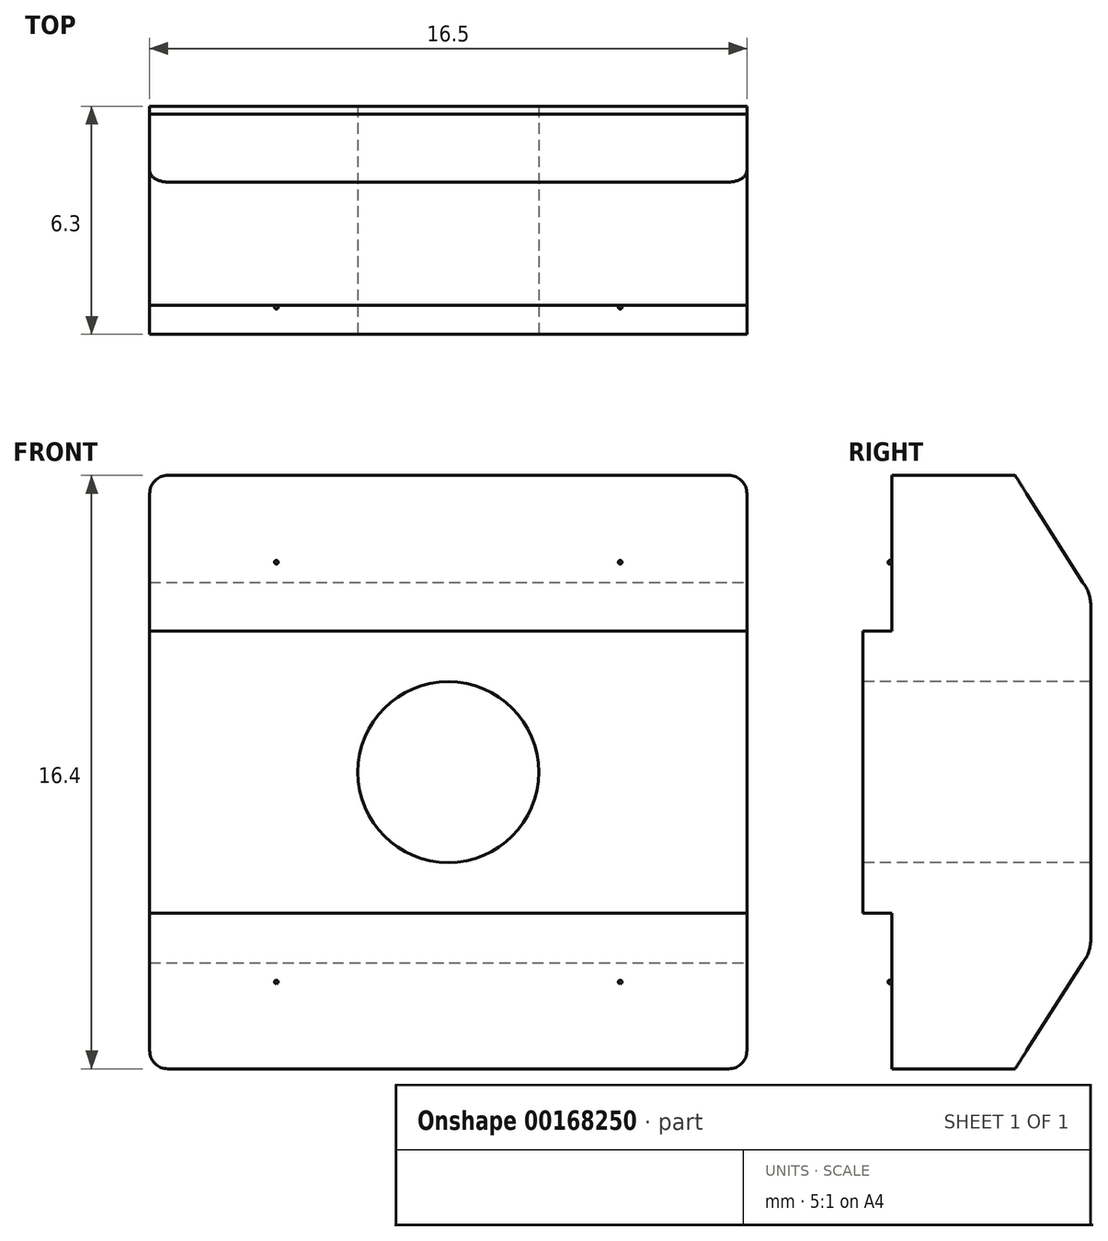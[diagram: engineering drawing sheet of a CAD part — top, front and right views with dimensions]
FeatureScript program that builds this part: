
annotation { "Feature Type Name" : "Feature", "Feature Type Description" : "" }
export const myFeature = defineFeature(function(context is Context, id is Id, definition is map)
    precondition{}
    {
        {
            var Q0;
            Q0=qCreatedBy(makeId("Front.planeOp"),FACE);
            var sketch = newSketch(context, id + "F0", { "sketchPlane" : qUnion([Q0])});
            skLineSegment(sketch, "E0", {"start": v(-32.08, -36.88) * mm, "end": v(-18.08, -36.88) * mm});
            skCircle(sketch, "E1", {"center": v(-25.08, -44.38) * mm, "radius": 1.5 * mm});
            skLineSegment(sketch, "E2", {"start": v(-32.08, -40.48) * mm, "end": v(-18.08, -40.48) * mm});
            skLineSegment(sketch, "E3", {"start": v(-32.08, -48.28) * mm, "end": v(-18.08, -48.28) * mm});
            skLineSegment(sketch, "E4", {"start": v(-18.08, -51.88) * mm, "end": v(-32.08, -51.88) * mm});
            skLineSegment(sketch, "E5", {"start": v(-35.33, -44.38) * mm, "end": v(-14.83, -44.38) * mm});
            skLineSegment(sketch, "E6", {"start": v(-32.08, -51.88) * mm, "end": v(-32.08, -36.88) * mm});
            skLineSegment(sketch, "E7", {"start": v(-25.08, -34.18) * mm, "end": v(-25.08, -54.58) * mm});
            skCircle(sketch, "E8", {"center": v(-25.08, -44.38) * mm, "radius": 1.23 * mm});
            skLineSegment(sketch, "E9", {"start": v(-18.08, -51.88) * mm, "end": v(-18.08, -36.88) * mm});
            skLineSegment(sketch, "E10", {"start": v(-33.33, -52.08) * mm, "end": v(-33.33, -36.68) * mm});
            skLineSegment(sketch, "E11", {"start": v(-16.83, -36.68) * mm, "end": v(-16.83, -52.08) * mm});
            skLineSegment(sketch, "E12", {"start": v(-17.33, -52.58) * mm, "end": v(-32.83, -52.58) * mm});
            skLineSegment(sketch, "E13", {"start": v(-32.83, -36.18) * mm, "end": v(-17.33, -36.18) * mm});
            skArc(sketch, "E14", {"start": v(-33.33, -52.08) * mm, "mid": v(-33.19, -52.43) * mm, "end": v(-32.83, -52.58) * mm});
            skArc(sketch, "E15", {"start": v(-17.33, -52.58) * mm, "mid": v(-16.98, -52.43) * mm, "end": v(-16.83, -52.08) * mm});
            skArc(sketch, "E16", {"start": v(-16.83, -36.68) * mm, "mid": v(-16.98, -36.33) * mm, "end": v(-17.33, -36.18) * mm});
            skArc(sketch, "E17", {"start": v(-32.83, -36.18) * mm, "mid": v(-33.19, -36.33) * mm, "end": v(-33.33, -36.68) * mm});
            skArc(sketch, "E18", {"start": v(27.03, -48.08) * mm, "mid": v(27.1, -48.22) * mm, "end": v(27.23, -48.28) * mm});
            skLineSegment(sketch, "E19", {"start": v(27.83, -52.58) * mm, "end": v(27.83, -36.18) * mm});
            skLineSegment(sketch, "E20", {"start": v(31.24, -36.18) * mm, "end": v(31.24, -52.58) * mm});
            skLineSegment(sketch, "E21", {"start": v(33.33, -49.02) * mm, "end": v(33.33, -39.76) * mm});
            skLineSegment(sketch, "E22", {"start": v(31.54, -51.6) * mm, "end": v(33.11, -49.65) * mm});
            skArc(sketch, "E23", {"start": v(33.11, -49.65) * mm, "mid": v(33.28, -49.35) * mm, "end": v(33.33, -49.02) * mm});
            skLineSegment(sketch, "E24", {"start": v(27.83, -52.58) * mm, "end": v(31.24, -52.58) * mm});
            skArc(sketch, "E25", {"start": v(31.24, -51.86) * mm, "mid": v(31.4, -51.75) * mm, "end": v(31.54, -51.6) * mm});
            skLineSegment(sketch, "E26", {"start": v(27.83, -48.28) * mm, "end": v(27.23, -48.28) * mm});
            skLineSegment(sketch, "E27", {"start": v(33.11, -39.13) * mm, "end": v(31.54, -37.16) * mm});
            skLineSegment(sketch, "E28", {"start": v(35.33, -44.38) * mm, "end": v(25.03, -44.38) * mm});
            skArc(sketch, "E29", {"start": v(33.33, -39.76) * mm, "mid": v(33.28, -39.43) * mm, "end": v(33.11, -39.13) * mm});
            skLineSegment(sketch, "E30", {"start": v(27.03, -48.08) * mm, "end": v(27.03, -40.68) * mm});
            skLineSegment(sketch, "E31", {"start": v(27.83, -36.18) * mm, "end": v(31.24, -36.18) * mm});
            skArc(sketch, "E32", {"start": v(31.54, -37.16) * mm, "mid": v(31.4, -37.02) * mm, "end": v(31.24, -36.9) * mm});
            skArc(sketch, "E33", {"start": v(27.23, -40.48) * mm, "mid": v(27.1, -40.54) * mm, "end": v(27.03, -40.68) * mm});
            skLineSegment(sketch, "E34", {"start": v(27.83, -40.48) * mm, "end": v(27.23, -40.48) * mm});
            skArc(sketch, "E35", {"start": v(27.03, -13.08) * mm, "mid": v(27.1, -13.22) * mm, "end": v(27.23, -13.28) * mm});
            skLineSegment(sketch, "E36", {"start": v(27.83, -17.58) * mm, "end": v(27.83, -1.18) * mm});
            skLineSegment(sketch, "E37", {"start": v(31.24, -1.18) * mm, "end": v(31.24, -17.58) * mm});
            skLineSegment(sketch, "E38", {"start": v(33.33, -14.02) * mm, "end": v(33.33, -4.76) * mm});
            skArc(sketch, "E39", {"start": v(31.24, -16.86) * mm, "mid": v(31.4, -16.75) * mm, "end": v(31.54, -16.6) * mm});
            skLineSegment(sketch, "E40", {"start": v(27.83, -13.28) * mm, "end": v(27.23, -13.28) * mm});
            skLineSegment(sketch, "E41", {"start": v(27.83, -17.58) * mm, "end": v(31.24, -17.58) * mm});
            skLineSegment(sketch, "E42", {"start": v(31.54, -16.6) * mm, "end": v(33.11, -14.65) * mm});
            skArc(sketch, "E43", {"start": v(33.11, -14.65) * mm, "mid": v(33.28, -14.35) * mm, "end": v(33.33, -14.02) * mm});
            skArc(sketch, "E44", {"start": v(31.54, -2.16) * mm, "mid": v(31.4, -2.02) * mm, "end": v(31.24, -1.9) * mm});
            skLineSegment(sketch, "E45", {"start": v(35.33, -9.38) * mm, "end": v(25.03, -9.38) * mm});
            skLineSegment(sketch, "E46", {"start": v(27.03, -13.08) * mm, "end": v(27.03, -5.68) * mm});
            skArc(sketch, "E47", {"start": v(27.23, -5.48) * mm, "mid": v(27.1, -5.54) * mm, "end": v(27.03, -5.68) * mm});
            skLineSegment(sketch, "E48", {"start": v(27.83, -5.48) * mm, "end": v(27.23, -5.48) * mm});
            skLineSegment(sketch, "E49", {"start": v(27.83, -1.18) * mm, "end": v(31.24, -1.18) * mm});
            skLineSegment(sketch, "E50", {"start": v(33.11, -4.13) * mm, "end": v(31.54, -2.16) * mm});
            skArc(sketch, "E51", {"start": v(33.33, -4.76) * mm, "mid": v(33.28, -4.43) * mm, "end": v(33.11, -4.13) * mm});
            skLineSegment(sketch, "E52", {"start": v(-25.08, 0.82) * mm, "end": v(-25.08, -19.58) * mm});
            skLineSegment(sketch, "E53", {"start": v(-32.83, -1.18) * mm, "end": v(-17.33, -1.18) * mm});
            skLineSegment(sketch, "E54", {"start": v(-17.33, -17.58) * mm, "end": v(-32.83, -17.58) * mm});
            skLineSegment(sketch, "E55", {"start": v(-35.33, -9.38) * mm, "end": v(-14.83, -9.38) * mm});
            skLineSegment(sketch, "E56", {"start": v(-18.08, -16.88) * mm, "end": v(-32.08, -16.88) * mm});
            skLineSegment(sketch, "E57", {"start": v(-32.08, -13.28) * mm, "end": v(-18.08, -13.28) * mm});
            skLineSegment(sketch, "E58", {"start": v(-32.08, -5.48) * mm, "end": v(-18.08, -5.48) * mm});
            skLineSegment(sketch, "E59", {"start": v(-32.08, -1.88) * mm, "end": v(-18.08, -1.88) * mm});
            skLineSegment(sketch, "E60", {"start": v(-33.33, -17.08) * mm, "end": v(-33.33, -1.68) * mm});
            skLineSegment(sketch, "E61", {"start": v(-32.08, -16.88) * mm, "end": v(-32.08, -1.88) * mm});
            skArc(sketch, "E62", {"start": v(-33.33, -17.08) * mm, "mid": v(-33.19, -17.43) * mm, "end": v(-32.83, -17.58) * mm});
            skArc(sketch, "E63", {"start": v(-32.83, -1.18) * mm, "mid": v(-33.19, -1.33) * mm, "end": v(-33.33, -1.68) * mm});
            skLineSegment(sketch, "E64", {"start": v(-16.83, -1.68) * mm, "end": v(-16.83, -17.08) * mm});
            skLineSegment(sketch, "E65", {"start": v(-18.08, -16.88) * mm, "end": v(-18.08, -1.88) * mm});
            skArc(sketch, "E66", {"start": v(-17.33, -17.58) * mm, "mid": v(-16.98, -17.43) * mm, "end": v(-16.83, -17.08) * mm});
            skCircle(sketch, "E67", {"center": v(-25.08, -9.38) * mm, "radius": 2 * mm});
            skCircle(sketch, "E68", {"center": v(-25.08, -9.38) * mm, "radius": 1.62 * mm});
            skArc(sketch, "E69", {"start": v(-16.83, -1.68) * mm, "mid": v(-16.98, -1.33) * mm, "end": v(-17.33, -1.18) * mm});
            skArc(sketch, "E70", {"start": v(27.03, 21.92) * mm, "mid": v(27.1, 21.78) * mm, "end": v(27.23, 21.72) * mm});
            skLineSegment(sketch, "E71", {"start": v(27.83, 17.42) * mm, "end": v(27.83, 33.82) * mm});
            skLineSegment(sketch, "E72", {"start": v(31.24, 33.82) * mm, "end": v(31.24, 17.42) * mm});
            skLineSegment(sketch, "E73", {"start": v(33.33, 20.98) * mm, "end": v(33.33, 30.24) * mm});
            skArc(sketch, "E74", {"start": v(31.24, 18.14) * mm, "mid": v(31.4, 18.25) * mm, "end": v(31.54, 18.4) * mm});
            skLineSegment(sketch, "E75", {"start": v(27.83, 21.72) * mm, "end": v(27.23, 21.72) * mm});
            skLineSegment(sketch, "E76", {"start": v(27.83, 17.42) * mm, "end": v(31.24, 17.42) * mm});
            skLineSegment(sketch, "E77", {"start": v(31.54, 18.4) * mm, "end": v(33.11, 20.35) * mm});
            skArc(sketch, "E78", {"start": v(33.11, 20.35) * mm, "mid": v(33.28, 20.65) * mm, "end": v(33.33, 20.98) * mm});
            skArc(sketch, "E79", {"start": v(31.54, 32.84) * mm, "mid": v(31.4, 32.98) * mm, "end": v(31.24, 33.1) * mm});
            skLineSegment(sketch, "E80", {"start": v(33.33, 28.12) * mm, "end": v(27.03, 28.12) * mm});
            skLineSegment(sketch, "E81", {"start": v(35.33, 25.62) * mm, "end": v(25.03, 25.62) * mm});
            skLineSegment(sketch, "E82", {"start": v(33.33, 23.12) * mm, "end": v(27.03, 23.12) * mm});
            skLineSegment(sketch, "E83", {"start": v(33.33, 27.69) * mm, "end": v(27.03, 27.69) * mm});
            skLineSegment(sketch, "E84", {"start": v(33.33, 23.55) * mm, "end": v(27.03, 23.55) * mm});
            skLineSegment(sketch, "E85", {"start": v(27.03, 21.92) * mm, "end": v(27.03, 29.32) * mm});
            skArc(sketch, "E86", {"start": v(27.23, 29.52) * mm, "mid": v(27.1, 29.46) * mm, "end": v(27.03, 29.32) * mm});
            skLineSegment(sketch, "E87", {"start": v(27.83, 29.52) * mm, "end": v(27.23, 29.52) * mm});
            skLineSegment(sketch, "E88", {"start": v(27.83, 33.82) * mm, "end": v(31.24, 33.82) * mm});
            skLineSegment(sketch, "E89", {"start": v(33.11, 30.87) * mm, "end": v(31.54, 32.84) * mm});
            skArc(sketch, "E90", {"start": v(33.33, 30.24) * mm, "mid": v(33.28, 30.57) * mm, "end": v(33.11, 30.87) * mm});
            skLineSegment(sketch, "E91", {"start": v(-25.08, 35.82) * mm, "end": v(-25.08, 15.42) * mm});
            skLineSegment(sketch, "E92", {"start": v(-32.83, 33.82) * mm, "end": v(-17.33, 33.82) * mm});
            skLineSegment(sketch, "E93", {"start": v(-17.33, 17.42) * mm, "end": v(-32.83, 17.42) * mm});
            skLineSegment(sketch, "E94", {"start": v(-35.33, 25.62) * mm, "end": v(-14.83, 25.62) * mm});
            skLineSegment(sketch, "E95", {"start": v(-18.08, 18.12) * mm, "end": v(-32.08, 18.12) * mm});
            skLineSegment(sketch, "E96", {"start": v(-32.08, 21.72) * mm, "end": v(-18.08, 21.72) * mm});
            skLineSegment(sketch, "E97", {"start": v(-32.08, 29.52) * mm, "end": v(-18.08, 29.52) * mm});
            skLineSegment(sketch, "E98", {"start": v(-32.08, 33.12) * mm, "end": v(-18.08, 33.12) * mm});
            skLineSegment(sketch, "E99", {"start": v(-33.33, 17.92) * mm, "end": v(-33.33, 33.32) * mm});
            skLineSegment(sketch, "E100", {"start": v(-32.08, 18.12) * mm, "end": v(-32.08, 33.12) * mm});
            skArc(sketch, "E101", {"start": v(-33.33, 17.92) * mm, "mid": v(-33.19, 17.57) * mm, "end": v(-32.83, 17.42) * mm});
            skArc(sketch, "E102", {"start": v(-32.83, 33.82) * mm, "mid": v(-33.19, 33.67) * mm, "end": v(-33.33, 33.32) * mm});
            skLineSegment(sketch, "E103", {"start": v(-16.83, 33.32) * mm, "end": v(-16.83, 17.92) * mm});
            skLineSegment(sketch, "E104", {"start": v(-18.08, 18.12) * mm, "end": v(-18.08, 33.12) * mm});
            skArc(sketch, "E105", {"start": v(-17.33, 17.42) * mm, "mid": v(-16.98, 17.57) * mm, "end": v(-16.83, 17.92) * mm});
            skCircle(sketch, "E106", {"center": v(-25.08, 25.62) * mm, "radius": 2.5 * mm});
            skCircle(sketch, "E107", {"center": v(-25.08, 25.62) * mm, "radius": 2.07 * mm});
            skArc(sketch, "E108", {"start": v(-16.83, 33.32) * mm, "mid": v(-16.98, 33.67) * mm, "end": v(-17.33, 33.82) * mm});
            skArc(sketch, "E109", {"start": v(27.03, 56.92) * mm, "mid": v(27.1, 56.78) * mm, "end": v(27.23, 56.72) * mm});
            skLineSegment(sketch, "E110", {"start": v(27.83, 52.42) * mm, "end": v(27.83, 68.82) * mm});
            skLineSegment(sketch, "E111", {"start": v(31.24, 68.82) * mm, "end": v(31.24, 52.42) * mm});
            skLineSegment(sketch, "E112", {"start": v(33.33, 55.98) * mm, "end": v(33.33, 65.24) * mm});
            skArc(sketch, "E113", {"start": v(31.24, 53.14) * mm, "mid": v(31.4, 53.25) * mm, "end": v(31.54, 53.4) * mm});
            skLineSegment(sketch, "E114", {"start": v(27.83, 56.72) * mm, "end": v(27.23, 56.72) * mm});
            skLineSegment(sketch, "E115", {"start": v(27.83, 52.42) * mm, "end": v(31.24, 52.42) * mm});
            skLineSegment(sketch, "E116", {"start": v(31.54, 53.4) * mm, "end": v(33.11, 55.35) * mm});
            skArc(sketch, "E117", {"start": v(33.11, 55.35) * mm, "mid": v(33.28, 55.65) * mm, "end": v(33.33, 55.98) * mm});
            skArc(sketch, "E118", {"start": v(31.54, 67.84) * mm, "mid": v(31.4, 67.98) * mm, "end": v(31.24, 68.1) * mm});
            skLineSegment(sketch, "E119", {"start": v(35.33, 60.62) * mm, "end": v(25.03, 60.62) * mm});
            skLineSegment(sketch, "E120", {"start": v(33.33, 57.62) * mm, "end": v(27.03, 57.62) * mm});
            skLineSegment(sketch, "E121", {"start": v(33.33, 58.16) * mm, "end": v(27.03, 58.16) * mm});
            skLineSegment(sketch, "E122", {"start": v(27.03, 56.92) * mm, "end": v(27.03, 64.32) * mm});
            skArc(sketch, "E123", {"start": v(27.23, 64.52) * mm, "mid": v(27.1, 64.46) * mm, "end": v(27.03, 64.32) * mm});
            skLineSegment(sketch, "E124", {"start": v(27.83, 64.52) * mm, "end": v(27.23, 64.52) * mm});
            skLineSegment(sketch, "E125", {"start": v(27.83, 68.82) * mm, "end": v(31.24, 68.82) * mm});
            skLineSegment(sketch, "E126", {"start": v(33.11, 65.87) * mm, "end": v(31.54, 67.84) * mm});
            skArc(sketch, "E127", {"start": v(33.33, 65.24) * mm, "mid": v(33.28, 65.57) * mm, "end": v(33.11, 65.87) * mm});
            skLineSegment(sketch, "E128", {"start": v(-25.08, 70.82) * mm, "end": v(-25.08, 50.42) * mm});
            skLineSegment(sketch, "E129", {"start": v(-32.83, 68.82) * mm, "end": v(-17.33, 68.82) * mm});
            skLineSegment(sketch, "E130", {"start": v(-17.33, 52.42) * mm, "end": v(-32.83, 52.42) * mm});
            skLineSegment(sketch, "E131", {"start": v(-35.33, 60.62) * mm, "end": v(-14.83, 60.62) * mm});
            skLineSegment(sketch, "E132", {"start": v(-18.08, 53.12) * mm, "end": v(-32.08, 53.12) * mm});
            skLineSegment(sketch, "E133", {"start": v(-32.08, 56.72) * mm, "end": v(-18.08, 56.72) * mm});
            skLineSegment(sketch, "E134", {"start": v(-32.08, 64.52) * mm, "end": v(-18.08, 64.52) * mm});
            skLineSegment(sketch, "E135", {"start": v(-32.08, 68.12) * mm, "end": v(-18.08, 68.12) * mm});
            skLineSegment(sketch, "E136", {"start": v(-33.33, 52.92) * mm, "end": v(-33.33, 68.32) * mm});
            skLineSegment(sketch, "E137", {"start": v(-32.08, 53.12) * mm, "end": v(-32.08, 68.12) * mm});
            skArc(sketch, "E138", {"start": v(-33.33, 52.92) * mm, "mid": v(-33.19, 52.57) * mm, "end": v(-32.83, 52.42) * mm});
            skArc(sketch, "E139", {"start": v(-32.83, 68.82) * mm, "mid": v(-33.19, 68.67) * mm, "end": v(-33.33, 68.32) * mm});
            skLineSegment(sketch, "E140", {"start": v(-16.83, 68.32) * mm, "end": v(-16.83, 52.92) * mm});
            skLineSegment(sketch, "E141", {"start": v(-18.08, 53.12) * mm, "end": v(-18.08, 68.12) * mm});
            skArc(sketch, "E142", {"start": v(-17.33, 52.42) * mm, "mid": v(-16.98, 52.57) * mm, "end": v(-16.83, 52.92) * mm});
            skCircle(sketch, "E143", {"center": v(-25.08, 60.62) * mm, "radius": 3 * mm});
            skCircle(sketch, "E144", {"center": v(-25.08, 60.62) * mm, "radius": 2.46 * mm});
            skArc(sketch, "E145", {"start": v(-16.83, 68.32) * mm, "mid": v(-16.98, 68.67) * mm, "end": v(-17.33, 68.82) * mm});
            skLineSegment(sketch, "E146", {"start": v(33.33, 63.08) * mm, "end": v(27.03, 63.08) * mm});
            skLineSegment(sketch, "E147", {"start": v(33.33, 63.62) * mm, "end": v(27.03, 63.62) * mm});
            skLineSegment(sketch, "E148", {"start": v(33.33, -7.76) * mm, "end": v(27.03, -7.76) * mm});
            skLineSegment(sketch, "E149", {"start": v(33.33, -7.38) * mm, "end": v(27.03, -7.38) * mm});
            skLineSegment(sketch, "E150", {"start": v(33.33, -11.38) * mm, "end": v(27.03, -11.38) * mm});
            skLineSegment(sketch, "E151", {"start": v(33.33, -11) * mm, "end": v(27.03, -11) * mm});
            skLineSegment(sketch, "E152", {"start": v(33.33, -45.61) * mm, "end": v(27.03, -45.61) * mm});
            skLineSegment(sketch, "E153", {"start": v(33.33, -45.88) * mm, "end": v(27.03, -45.88) * mm});
            skLineSegment(sketch, "E154", {"start": v(33.33, -43.15) * mm, "end": v(27.03, -43.15) * mm});
            skLineSegment(sketch, "E155", {"start": v(33.33, -42.88) * mm, "end": v(27.03, -42.88) * mm});
            skSolve(sketch);
        }
        {
            var Q0;
            Q0=qCreatedBy(makeId("Front.planeOp"),FACE);
            var sketch = newSketch(context, id + "F1", { "sketchPlane" : qUnion([Q0])});
            skLineSegment(sketch, "E156.0", {"start": v(7.75, -8.2) * mm, "end": v(-7.75, -8.2) * mm});
            skLineSegment(sketch, "E156.2", {"start": v(7, -7.5) * mm, "end": v(-7, -7.5) * mm});
            skLineSegment(sketch, "E156.3", {"start": v(-7, -3.9) * mm, "end": v(7, -3.9) * mm});
            skLineSegment(sketch, "E156.4", {"start": v(-7, 3.9) * mm, "end": v(7, 3.9) * mm});
            skLineSegment(sketch, "E156.5", {"start": v(-7, 7.5) * mm, "end": v(7, 7.5) * mm});
            skLineSegment(sketch, "E156.6", {"start": v(-8.25, -7.7) * mm, "end": v(-8.25, 7.7) * mm});
            skLineSegment(sketch, "E156.7", {"start": v(-7, -7.5) * mm, "end": v(-7, 7.5) * mm});
            skLineSegment(sketch, "E156.8", {"start": v(8.25, 7.7) * mm, "end": v(8.25, -7.7) * mm});
            skLineSegment(sketch, "E156.9", {"start": v(7, -7.5) * mm, "end": v(7, 7.5) * mm});
            skCircle(sketch, "E156.10", {"center": v(0, 0) * mm, "radius": 2.5 * mm});
            skCircle(sketch, "E156.11", {"center": v(0, 0) * mm, "radius": 2.07 * mm});
            skLineSegment(sketch, "E156.13", {"start": v(-7.75, 8.2) * mm, "end": v(7.75, 8.2) * mm});
            skArc(sketch, "E156.14", {"start": v(8.25, 7.7) * mm, "mid": v(8.1, 8.05) * mm, "end": v(7.75, 8.2) * mm});
            skArc(sketch, "E156.15", {"start": v(-7.75, 8.2) * mm, "mid": v(-8.1, 8.05) * mm, "end": v(-8.25, 7.7) * mm});
            skArc(sketch, "E156.16", {"start": v(7.75, -8.2) * mm, "mid": v(8.1, -8.05) * mm, "end": v(8.25, -7.7) * mm});
            skArc(sketch, "E156.17", {"start": v(-8.25, -7.7) * mm, "mid": v(-8.1, -8.05) * mm, "end": v(-7.75, -8.2) * mm});
            skSolve(sketch);
        }
        {
            var Q0;
            Q0 = qSketchRegion(id + "F1", true);
            var Q1;
            {var subQ0=sQuery(id+"F1.wireOp",EDGE,"E156.4");Q1=makeQuery(id+"F1.imprint","IMPRINT",FACE,{"disambiguationData":[TD([[makeQuery(id+"F1.imprint","IMPRINT",EDGE,{"derivedFrom":subQ0}),1.0]])]});}
            var Q2;
            {var subQ0=sQuery(id+"F1.wireOp",EDGE,"E156.2");Q2=makeQuery(id+"F1.imprint","IMPRINT",FACE,{"disambiguationData":[TD([[makeQuery(id+"F1.imprint","IMPRINT",EDGE,{"derivedFrom":subQ0}),-1.0]])]});}
            var Q3;
            {var subQ1=sQuery(id+"F1.wireOp",EDGE,"E156.3");Q3=makeQuery(id+"F1.imprint","IMPRINT",FACE,{"disambiguationData":[TD([[makeQuery(id+"F1.imprint","IMPRINT",EDGE,{"derivedFrom":subQ1}),1.0]])]});}
            var Q4;
            Q4=makeQuery(id+"F1.imprint","IMPRINT",FACE,{"disambiguationData":[TD([[makeQuery(id+"F1.imprint","IMPRINT",EDGE,{"derivedFrom":sQuery(id+"F1.wireOp",EDGE,"E156.10")}),-1.0]])]});
            extrude(context, id + "F2", {"entities" : qUnion([Q0, Q1, Q2, Q3, Q4]), "oppositeDirection" : true, "depth" : 6.3 * mm});
        }
        {
            var Q0;
            Q0=qCreatedBy(makeId("Front.planeOp"),FACE);
            var sketch = newSketch(context, id + "F3", { "sketchPlane" : qUnion([Q0])});
            skLineSegment(sketch, "E157.0", {"start": v(-8.25, -7.7) * mm, "end": v(-8.25, 7.7) * mm});
            skLineSegment(sketch, "E158.0", {"start": v(8.25, 7.7) * mm, "end": v(8.25, -7.7) * mm});
            skLineSegment(sketch, "E159.0", {"start": v(-7.75, 8.2) * mm, "end": v(7.75, 8.2) * mm});
            skLineSegment(sketch, "E160.0", {"start": v(7.75, -8.2) * mm, "end": v(-7.75, -8.2) * mm});
            skArc(sketch, "E161.0", {"start": v(7.75, -8.2) * mm, "mid": v(8.1, -8.05) * mm, "end": v(8.25, -7.7) * mm});
            skLineSegment(sketch, "E162.0", {"start": v(-7, -3.9) * mm, "end": v(7, -3.9) * mm});
            skLineSegment(sketch, "E163.0", {"start": v(-7, 3.9) * mm, "end": v(7, 3.9) * mm});
            skArc(sketch, "E164.0", {"start": v(8.25, 7.7) * mm, "mid": v(8.1, 8.05) * mm, "end": v(7.75, 8.2) * mm});
            skArc(sketch, "E165.0", {"start": v(-7.75, 8.2) * mm, "mid": v(-8.1, 8.05) * mm, "end": v(-8.25, 7.7) * mm});
            skArc(sketch, "E166.0", {"start": v(-8.25, -7.7) * mm, "mid": v(-8.1, -8.05) * mm, "end": v(-7.75, -8.2) * mm});
            skLineSegment(sketch, "E167", {"start": v(-8.25, 3.9) * mm, "end": v(-7, 3.9) * mm});
            skLineSegment(sketch, "E168", {"start": v(7, 3.9) * mm, "end": v(8.25, 3.9) * mm});
            skLineSegment(sketch, "E169", {"start": v(-7, -3.9) * mm, "end": v(-8.25, -3.9) * mm});
            skLineSegment(sketch, "E170", {"start": v(7, -3.9) * mm, "end": v(8.25, -3.9) * mm});
            skSolve(sketch);
        }
        {
            var Q0;
            Q0=makeQuery(id+"F3.imprint","IMPRINT",FACE,{"disambiguationData":[TD([[makeQuery(id+"F3.imprint","IMPRINT",EDGE,{"derivedFrom":sQuery(id+"F3.wireOp",EDGE,"E159.0")}),-1.0]])]});
            var Q1;
            Q1=makeQuery(id+"F3.imprint","IMPRINT",FACE,{"disambiguationData":[TD([[makeQuery(id+"F3.imprint","IMPRINT",EDGE,{"derivedFrom":sQuery(id+"F3.wireOp",EDGE,"E160.0")}),-1.0]])]});
            extrude(context, id + "F4", {"entities" : qUnion([Q0, Q1]), "operationType" : NewBodyOperationType.REMOVE, "oppositeDirection" : true, "depth" : 0.8 * mm});
        }
        {
            var Q0;
            Q0=qCreatedBy(makeId("Right.planeOp"),FACE);
            var sketch = newSketch(context, id + "F5", { "sketchPlane" : qUnion([Q0])});
            skLineSegment(sketch, "E171.0", {"start": v(6.47, 0) * mm, "end": v(6.3, 0) * mm});
            skLineSegment(sketch, "E171.3", {"start": v(6.3, -4.64) * mm, "end": v(6.3, 4.62) * mm});
            skLineSegment(sketch, "E171.11", {"start": v(4.51, -7.23) * mm, "end": v(4.51, -7.23) * mm});
            skArc(sketch, "E171.14", {"start": v(6.08, -5.27) * mm, "mid": v(6.24, -4.97) * mm, "end": v(6.3, -4.64) * mm});
            skArc(sketch, "E171.15", {"start": v(6.3, 4.62) * mm, "mid": v(6.24, 4.95) * mm, "end": v(6.08, 5.24) * mm});
            skLineSegment(sketch, "E172", {"start": v(4.21, 8.2) * mm, "end": v(6.47, 8.2) * mm});
            skLineSegment(sketch, "E173", {"start": v(6.47, 8.2) * mm, "end": v(6.47, -8.2) * mm});
            skLineSegment(sketch, "E174", {"start": v(6.47, -8.2) * mm, "end": v(4.21, -8.2) * mm});
            skLineSegment(sketch, "E175", {"start": v(4.21, 8.2) * mm, "end": v(6.08, 5.24) * mm});
            skLineSegment(sketch, "E176", {"start": v(4.21, -8.2) * mm, "end": v(6.08, -5.27) * mm});
            skSolve(sketch);
        }
        {
            var Q0;
            Q0 = qSketchRegion(id + "F5", true);
            extrude(context, id + "F6", {"entities" : qUnion([Q0]), "operationType" : NewBodyOperationType.REMOVE, "endBound" : BoundingType.SYMMETRIC, "oppositeDirection" : true, "depth" : 25 * mm});
        }
        {
            var Q0;
            Q0=makeQuery(id+"F4.boolean.opBoolean","COPY",FACE,{"derivedFrom":makeQuery(id+"F4.opExtrude","CAP_FACE",FACE,{"disambiguationData":[OSD([sQuery(id+"F3.wireOp",EDGE,"E157.0"),sQuery(id+"F3.wireOp",EDGE,"E158.0"),sQuery(id+"F3.wireOp",EDGE,"E159.0"),sQuery(id+"F3.wireOp",EDGE,"E163.0"),sQuery(id+"F3.wireOp",EDGE,"E164.0"),sQuery(id+"F3.wireOp",EDGE,"E165.0"),sQuery(id+"F3.wireOp",EDGE,"E167"),sQuery(id+"F3.wireOp",EDGE,"E168")])],"isStart":false})});
            var sketch = newSketch(context, id + "F7", { "sketchPlane" : qUnion([Q0])});
            skLineSegment(sketch, "E177.0", {"start": v(-8.25, 3.9) * mm, "end": v(-8.25, 7.7) * mm});
            skPoint(sketch, "E178.0", {"position": v(8.25, 5.8) * mm});
            skLineSegment(sketch, "E179.0", {"start": v(8.25, 7.7) * mm, "end": v(8.25, 3.9) * mm});
            skLineSegment(sketch, "E180.0", {"start": v(8.25, -3.9) * mm, "end": v(8.25, -7.7) * mm});
            skLineSegment(sketch, "E181.0", {"start": v(-8.25, -7.7) * mm, "end": v(-8.25, -3.9) * mm});
            skLineSegment(sketch, "E182", {"start": v(-8.25, 5.8) * mm, "end": v(8.25, 5.8) * mm, "construction": true});
            skLineSegment(sketch, "E183", {"start": v(-8.25, -5.8) * mm, "end": v(8.25, -5.8) * mm, "construction": true});
            skCircle(sketch, "E184", {"center": v(4.75, 5.8) * mm, "radius": 0.05 * mm});
            skLineSegment(sketch, "E185.0", {"start": v(-8.25, -3.9) * mm, "end": v(-8.25, 3.9) * mm, "construction": true});
            skLineSegment(sketch, "E186.0", {"start": v(8.25, 3.9) * mm, "end": v(8.25, -3.9) * mm, "construction": true});
            skLineSegment(sketch, "E187.0", {"start": v(-8.25, 0) * mm, "end": v(8.25, 0) * mm, "construction": true});
            skLineSegment(sketch, "E188.0", {"start": v(0, -3.9) * mm, "end": v(0, 3.9) * mm, "construction": true});
            skCircle(sketch, "E189.MirrorC", {"center": v(-4.75, 5.8) * mm, "radius": 0.05 * mm});
            skCircle(sketch, "E190.MirrorC", {"center": v(-4.75, -5.8) * mm, "radius": 0.05 * mm});
            skCircle(sketch, "E191.MirrorC", {"center": v(4.75, -5.8) * mm, "radius": 0.05 * mm});
            skSolve(sketch);
        }
        {
            var Q0;
            Q0 = qSketchRegion(id + "F7", true);
            extrude(context, id + "F8", {"entities" : qUnion([Q0]), "operationType" : NewBodyOperationType.ADD, "depth" : 0.1 * mm});
        }
        {
            var Q0;
            Q0=makeQuery(id+"F8.opExtrude","CAP_EDGE",EDGE,{"disambiguationData":[OSD([sQuery(id+"F7.wireOp",EDGE,"E190.MirrorC")])],"isStart":false});
            var Q1;
            Q1=makeQuery(id+"F8.opExtrude","CAP_EDGE",EDGE,{"disambiguationData":[OSD([sQuery(id+"F7.wireOp",EDGE,"E191.MirrorC")])],"isStart":false});
            var Q2;
            Q2=makeQuery(id+"F8.opExtrude","CAP_EDGE",EDGE,{"disambiguationData":[OSD([sQuery(id+"F7.wireOp",EDGE,"E184")])],"isStart":false});
            var Q3;
            Q3=makeQuery(id+"F8.opExtrude","CAP_EDGE",EDGE,{"disambiguationData":[OSD([sQuery(id+"F7.wireOp",EDGE,"E189.MirrorC")])],"isStart":false});
            fillet(context, id + "F9", {"entities" : qUnion([Q0, Q1, Q2, Q3]), "radius" : 0.05 * mm, "tangentPropagation" : true, "allowEdgeOverflow" : false});
        }
    });
